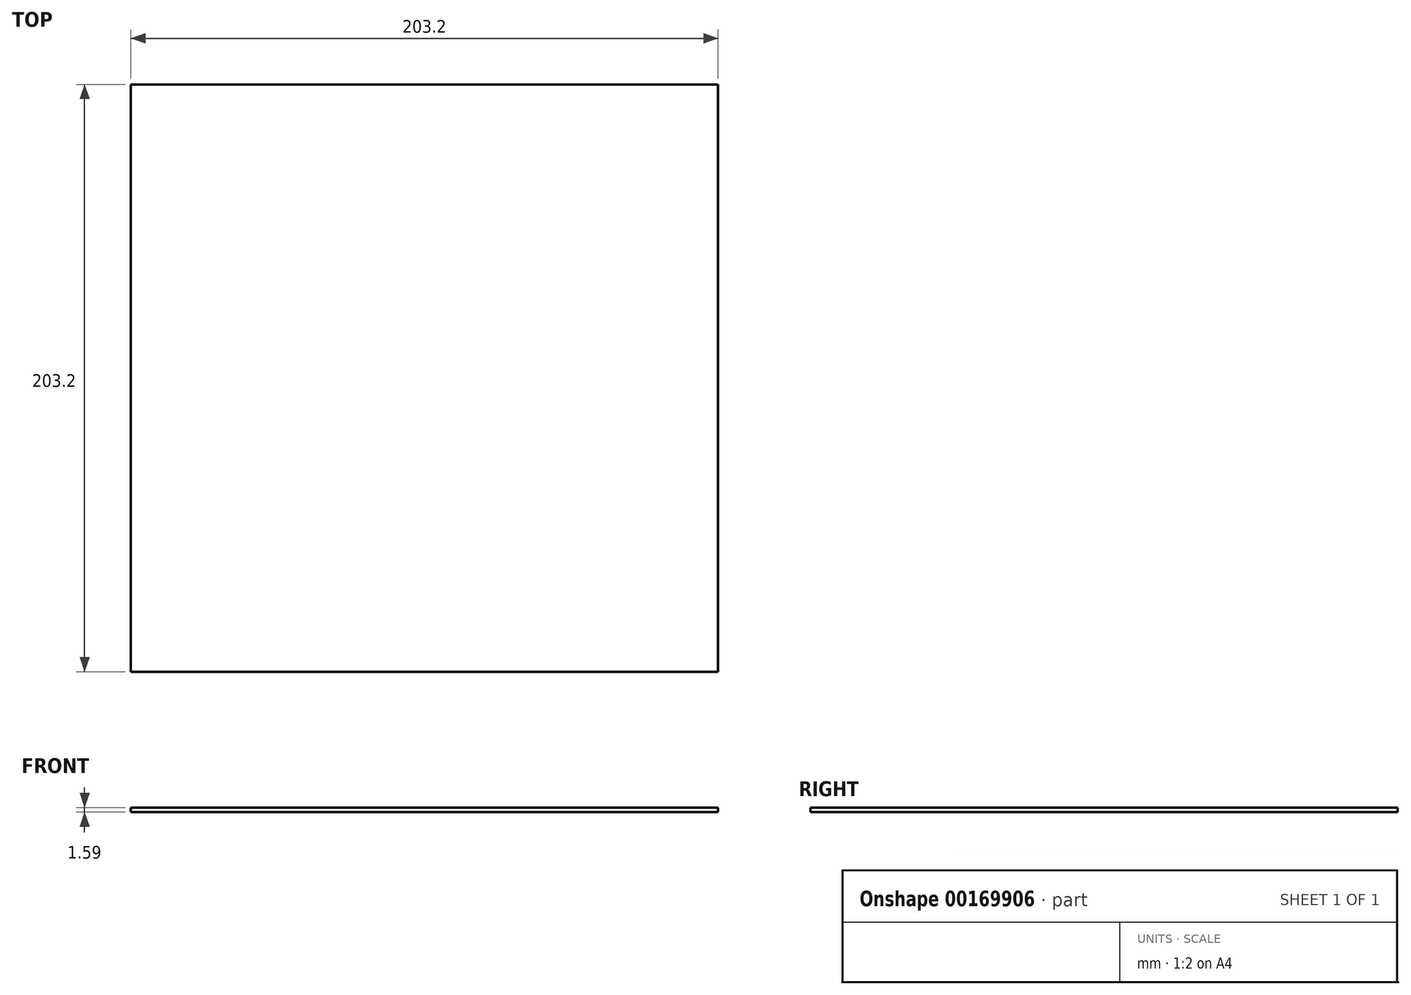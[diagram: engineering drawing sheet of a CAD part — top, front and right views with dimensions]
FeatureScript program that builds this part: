
annotation { "Feature Type Name" : "Feature", "Feature Type Description" : "" }
export const myFeature = defineFeature(function(context is Context, id is Id, definition is map)
    precondition{}
    {
        {
            var Q0;
            Q0=qCreatedBy(makeId("Top.planeOp"),FACE);
            var sketch = newSketch(context, id + "F0", { "sketchPlane" : qUnion([Q0])});
            skLineSegment(sketch, "E0.bottom", {"start": v(-100.66, 101.05) * mm, "end": v(102.54, 101.05) * mm});
            skLineSegment(sketch, "E0.top", {"start": v(-100.66, -102.15) * mm, "end": v(102.54, -102.15) * mm});
            skLineSegment(sketch, "E0.left", {"start": v(-100.66, 101.05) * mm, "end": v(-100.66, -102.15) * mm});
            skLineSegment(sketch, "E0.right", {"start": v(102.54, 101.05) * mm, "end": v(102.54, -102.15) * mm});
            skSolve(sketch);
        }
        {
            var Q0;
            Q0=makeQuery(id+"F0.imprint","IMPRINT",FACE,{"disambiguationData":[TD([[makeQuery(id+"F0.imprint","IMPRINT",EDGE,{"derivedFrom":sQuery(id+"F0.wireOp",EDGE,"E0.bottom")}),-1.0]])]});
            extrude(context, id + "F1", {"entities" : qUnion([Q0]), "depth" : 1.59 * mm});
        }
    });
